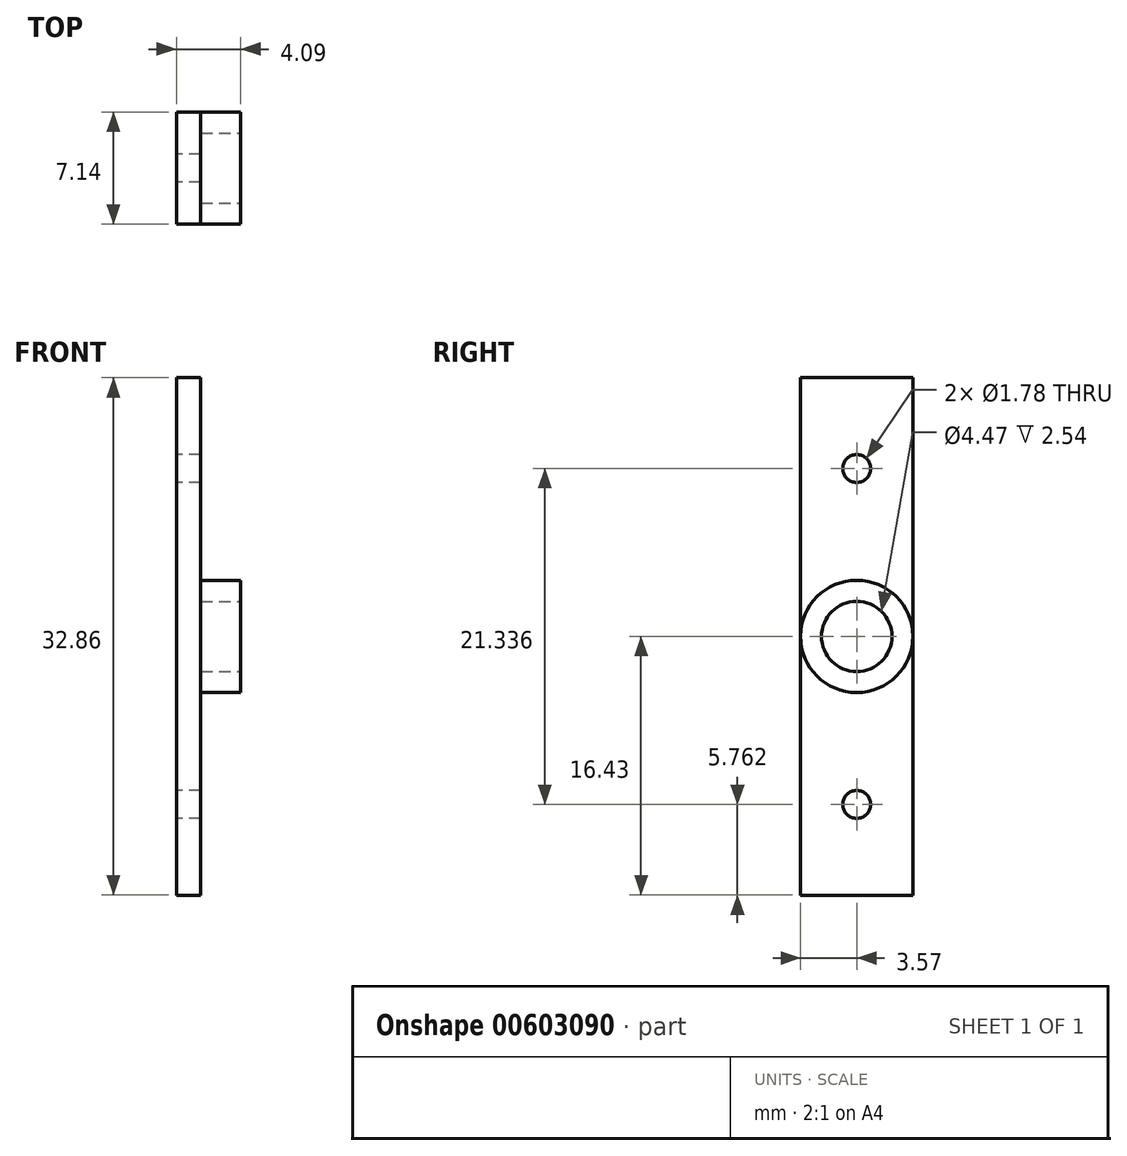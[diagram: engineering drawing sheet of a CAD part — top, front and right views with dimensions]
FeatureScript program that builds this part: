
annotation { "Feature Type Name" : "Feature", "Feature Type Description" : "" }
export const myFeature = defineFeature(function(context is Context, id is Id, definition is map)
    precondition{}
    {
        {
            var Q0;
            Q0=qCreatedBy(makeId("Right.planeOp"),FACE);
            var sketch = newSketch(context, id + "F0", { "sketchPlane" : qUnion([Q0])});
            skCircle(sketch, "E0", {"center": v(0, 0) * mm, "radius": 3.57 * mm});
            skSolve(sketch);
        }
        {
            var Q0;
            Q0 = qSketchRegion(id + "F0", true);
            extrude(context, id + "F1", {"entities" : qUnion([Q0]), "depth" : 2.54 * mm, "offsetDistance" : 25.4 * mm});
        }
        {
            var Q0;
            Q0=makeQuery(id+"F1.opExtrude","CAP_FACE",FACE,{"disambiguationData":[OSD([sQuery(id+"F0.wireOp",EDGE,"E0")])],"isStart":false});
            var sketch = newSketch(context, id + "F2", { "sketchPlane" : qUnion([Q0])});
            skCircle(sketch, "E1", {"center": v(0, 0) * mm, "radius": 2.24 * mm});
            skSolve(sketch);
        }
        {
            var Q0;
            Q0 = qSketchRegion(id + "F2", true);
            extrude(context, id + "F3", {"entities" : qUnion([Q0]), "operationType" : NewBodyOperationType.REMOVE, "oppositeDirection" : true, "depth" : 2.54 * mm, "offsetDistance" : 25.4 * mm});
        }
        {
            var Q0;
            Q0=qCreatedBy(makeId("Front.planeOp"),FACE);
            var sketch = newSketch(context, id + "F4", { "sketchPlane" : qUnion([Q0])});
            skLineSegment(sketch, "E2.bottom", {"start": v(0, 16.43) * mm, "end": v(-1.55, 16.43) * mm});
            skLineSegment(sketch, "E2.top", {"start": v(0, -16.43) * mm, "end": v(-1.55, -16.43) * mm});
            skLineSegment(sketch, "E2.left", {"start": v(0, 16.43) * mm, "end": v(0, -16.43) * mm});
            skLineSegment(sketch, "E2.right", {"start": v(-1.55, 16.43) * mm, "end": v(-1.55, -16.43) * mm});
            skSolve(sketch);
        }
        {
            var Q0;
            Q0 = qSketchRegion(id + "F4", true);
            extrude(context, id + "F5", {"entities" : qUnion([Q0]), "operationType" : NewBodyOperationType.ADD, "endBound" : BoundingType.SYMMETRIC, "depth" : 7.14 * mm, "offsetDistance" : 25.4 * mm});
        }
        {
            var Q0;
            Q0=makeQuery(id+"F5.opExtrude","SWEPT_FACE",FACE,{"disambiguationData":[OSD([sQuery(id+"F4.wireOp",EDGE,"E2.right")])]});
            var sketch = newSketch(context, id + "F6", { "sketchPlane" : qUnion([Q0])});
            skCircle(sketch, "E3", {"center": v(0, -10.67) * mm, "radius": 0.89 * mm});
            skCircle(sketch, "E4", {"center": v(0, 10.67) * mm, "radius": 0.89 * mm});
            skSolve(sketch);
        }
        {
            var Q0;
            Q0 = qSketchRegion(id + "F6", true);
            extrude(context, id + "F7", {"entities" : qUnion([Q0]), "operationType" : NewBodyOperationType.REMOVE, "oppositeDirection" : true, "depth" : 25.4 * mm, "offsetDistance" : 25.4 * mm});
        }
    });
